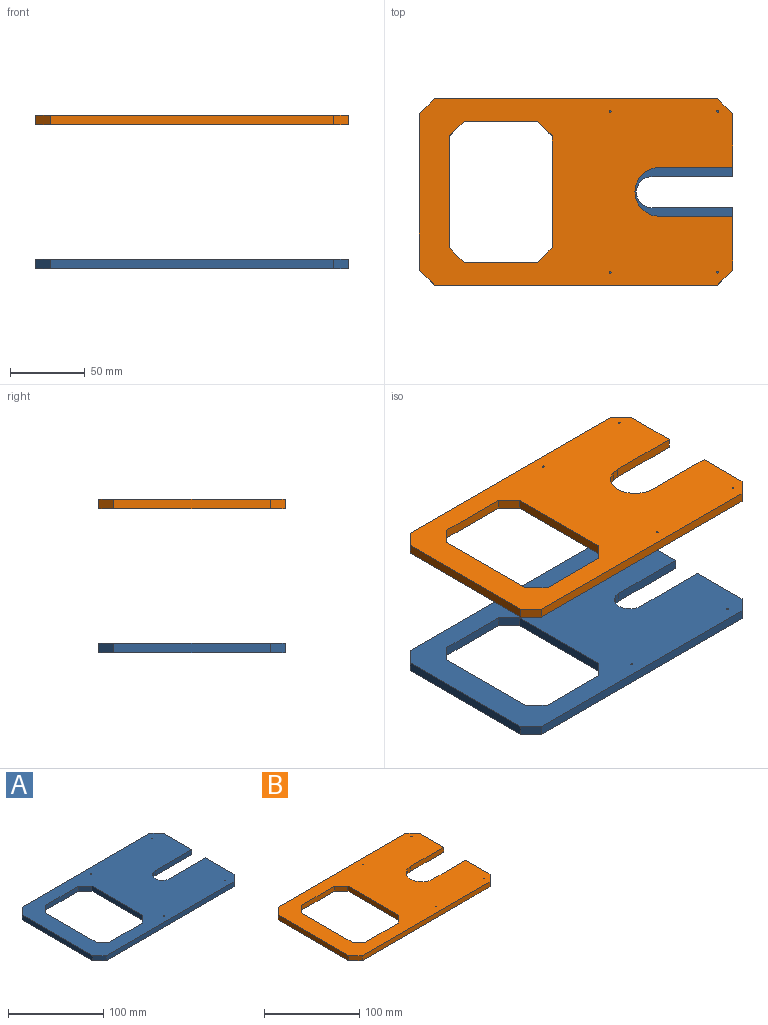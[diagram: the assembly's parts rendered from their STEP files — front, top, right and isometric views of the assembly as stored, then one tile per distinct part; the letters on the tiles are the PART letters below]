
ASSEMBLY  parts=2 mates=2
PART A: 73 faces, bbox 210x125x6.4 mm
  f0: plane 210x125mm, normal (0,0,1), area 18386mm2, adj f2,f3,f4,f5,f6,f7,f8,f9
  f1: plane 210x125mm, normal (0,0,-1), area 18386mm2, adj f2,f3,f4,f5,f6,f7,f8,f9
  f2: plane 42x6.4mm, normal (1,0,0), area 268.8mm2, adj f0,f1,f9,f63
  f3: plane 42x6.4mm, normal (1,0,0), area 268.8mm2, adj f0,f1,f8,f62
  f4: plane 190x6.4mm, normal (0,1,0), area 1216mm2, adj f0,f1,f63,f64
  f5: plane 105x6.4mm, normal (-1,0,0), area 672mm2, adj f0,f1,f61,f64
  f6: plane 190x6.4mm, normal (0,-1,0), area 1216mm2, adj f0,f1,f61,f62
  f7: plane 6.4x3.24mm, normal (0.16,0.99,0), area 21mm2, adj f0,f1,f8,f18
  f8: plane 54x6.4mm, normal (0,1,0), area 345.6mm2, adj f0,f1,f3,f7
  f9: plane 54x6.4mm, normal (0,-1,0), area 345.6mm2, adj f0,f1,f2,f10
  f10: plane 6.4x3.24mm, normal (0.16,-0.99,0), area 21mm2, adj f0,f1,f9,f11
  f11: plane 6.4x2.93mm, normal (0.45,-0.89,0), area 21mm2, adj f0,f1,f10,f12
  f12: plane 6.4x2.32mm, normal (0.71,-0.71,0), area 21mm2, adj f0,f1,f11,f13
  f13: plane 6.4x2.93mm, normal (0.89,-0.45,0), area 21mm2, adj f0,f1,f12,f14
  f14: plane 6.4x3.24mm, normal (0.99,-0.16,0), area 21mm2, adj f0,f1,f13,f15
  f15: plane 6.4x3.24mm, normal (0.99,0.16,0), area 21mm2, adj f0,f1,f14,f16
  f16: plane 6.4x2.93mm, normal (0.89,0.45,0), area 21mm2, adj f0,f1,f15,f17
  f17: plane 6.4x2.32mm, normal (0.71,0.71,0), area 21mm2, adj f0,f1,f16,f18
  f18: plane 6.4x2.93mm, normal (0.45,0.89,0), area 21mm2, adj f0,f1,f7,f17
  f19: plane 6.4x0.34mm, normal (-0.28,0.96,0), area 2.3mm2, adj f0,f1,f20,f29
  f20: plane 6.4x0.27mm, normal (-0.76,0.65,0), area 2.3mm2, adj f0,f1,f19,f21
  f21: plane 6.4x0.35mm, normal (-0.99,0.14,0), area 2.3mm2, adj f0,f1,f20,f22
  f22: plane 6.4x0.32mm, normal (-0.91,-0.42,0), area 2.3mm2, adj f0,f1,f21,f23
  f23: plane 6.4x0.3mm, normal (-0.54,-0.84,0), area 2.3mm2, adj f0,f1,f22,f24
  f24: plane 6.4x0.35mm, normal (0,-1,0), area 2.3mm2, adj f0,f1,f23,f25
  f25: plane 6.4x0.3mm, normal (0.54,-0.84,0), area 2.3mm2, adj f0,f1,f24,f26
  f26: plane 6.4x0.32mm, normal (0.91,-0.42,0), area 2.3mm2, adj f0,f1,f25,f27
  f27: plane 6.4x0.35mm, normal (0.99,0.14,0), area 2.3mm2, adj f0,f1,f26,f28
  f28: plane 6.4x0.27mm, normal (0.76,0.65,0), area 2.3mm2, adj f0,f1,f27,f29
  f29: plane 6.4x0.34mm, normal (0.28,0.96,0), area 2.3mm2, adj f0,f1,f19,f28
  f30: plane 6.4x0.37mm, normal (-0.31,0.95,0), area 2.5mm2, adj f0,f1,f31,f39
  f31: plane 6.4x0.32mm, normal (-0.81,0.59,0), area 2.5mm2, adj f0,f1,f30,f32
  f32: plane 6.4x0.39mm, normal (-1,0,0), area 2.5mm2, adj f0,f1,f31,f33
  f33: plane 6.4x0.32mm, normal (-0.81,-0.59,0), area 2.5mm2, adj f0,f1,f32,f34
  f34: plane 6.4x0.37mm, normal (-0.31,-0.95,0), area 2.5mm2, adj f0,f1,f33,f35
  f35: plane 6.4x0.37mm, normal (0.31,-0.95,0), area 2.5mm2, adj f0,f1,f34,f36
  f36: plane 6.4x0.32mm, normal (0.81,-0.59,0), area 2.5mm2, adj f0,f1,f35,f37
  f37: plane 6.4x0.39mm, normal (1,0,0), area 2.5mm2, adj f0,f1,f36,f38
  f38: plane 6.4x0.32mm, normal (0.81,0.59,0), area 2.5mm2, adj f0,f1,f37,f39
  f39: plane 6.4x0.37mm, normal (0.31,0.95,0), area 2.5mm2, adj f0,f1,f30,f38
  f40: plane 6.4x0.39mm, normal (-1,0,0), area 2.5mm2, adj f0,f1,f41,f49
  f41: plane 6.4x0.32mm, normal (-0.81,-0.59,0), area 2.5mm2, adj f0,f1,f40,f42
  f42: plane 6.4x0.37mm, normal (-0.31,-0.95,0), area 2.5mm2, adj f0,f1,f41,f43
  f43: plane 6.4x0.37mm, normal (0.31,-0.95,0), area 2.5mm2, adj f0,f1,f42,f44
  f44: plane 6.4x0.32mm, normal (0.81,-0.59,0), area 2.5mm2, adj f0,f1,f43,f45
  f45: plane 6.4x0.39mm, normal (1,0,0), area 2.5mm2, adj f0,f1,f44,f46
  f46: plane 6.4x0.32mm, normal (0.81,0.59,0), area 2.5mm2, adj f0,f1,f45,f47
  f47: plane 6.4x0.37mm, normal (0.31,0.95,0), area 2.5mm2, adj f0,f1,f46,f48
  f48: plane 6.4x0.37mm, normal (-0.31,0.95,0), area 2.5mm2, adj f0,f1,f47,f49
  f49: plane 6.4x0.32mm, normal (-0.81,0.59,0), area 2.5mm2, adj f0,f1,f40,f48
  f50: plane 6.4x0.27mm, normal (-0.76,-0.65,0), area 2.3mm2, adj f0,f1,f51,f60
  f51: plane 6.4x0.34mm, normal (-0.28,-0.96,0), area 2.3mm2, adj f0,f1,f50,f52
  f52: plane 6.4x0.34mm, normal (0.28,-0.96,0), area 2.3mm2, adj f0,f1,f51,f53
  f53: plane 6.4x0.27mm, normal (0.76,-0.65,0), area 2.3mm2, adj f0,f1,f52,f54
  f54: plane 6.4x0.35mm, normal (0.99,-0.14,0), area 2.3mm2, adj f0,f1,f53,f55
  f55: plane 6.4x0.32mm, normal (0.91,0.42,0), area 2.3mm2, adj f0,f1,f54,f56
  f56: plane 6.4x0.3mm, normal (0.54,0.84,0), area 2.3mm2, adj f0,f1,f55,f57
  f57: plane 6.4x0.35mm, normal (0,1,0), area 2.3mm2, adj f0,f1,f56,f58
  f58: plane 6.4x0.3mm, normal (-0.54,0.84,0), area 2.3mm2, adj f0,f1,f57,f59
  f59: plane 6.4x0.32mm, normal (-0.91,0.42,0), area 2.3mm2, adj f0,f1,f58,f60
  f60: plane 6.4x0.35mm, normal (-0.99,-0.14,0), area 2.3mm2, adj f0,f1,f50,f59
  f61: plane 10x10mm, normal (-0.71,-0.71,0), area 90.5mm2, adj f0,f1,f5,f6
  f62: plane 10x10mm, normal (0.71,-0.71,0), area 90.5mm2, adj f0,f1,f3,f6
  f63: plane 10x10mm, normal (0.71,0.71,0), area 90.5mm2, adj f0,f1,f2,f4
  f64: plane 10x10mm, normal (-0.71,0.71,0), area 90.5mm2, adj f0,f1,f4,f5
  f65: plane 75x6.4mm, normal (-1,0,0), area 480mm2, adj f0,f1,f70,f71
  f66: plane 49x6.4mm, normal (0,1,0), area 313.6mm2, adj f0,f1,f69,f70
  f67: plane 75x6.4mm, normal (1,0,0), area 480mm2, adj f0,f1,f69,f72
  f68: plane 49x6.4mm, normal (0,-1,0), area 313.6mm2, adj f0,f1,f71,f72
  f69: plane 10x10mm, normal (0.71,0.71,0), area 90.5mm2, adj f0,f1,f66,f67
  f70: plane 10x10mm, normal (-0.71,0.71,0), area 90.5mm2, adj f0,f1,f65,f66
  f71: plane 10x10mm, normal (-0.71,-0.71,0), area 90.5mm2, adj f0,f1,f65,f68
  f72: plane 10x10mm, normal (0.71,-0.71,0), area 90.5mm2, adj f0,f1,f67,f68
PART B: 73 faces, bbox 210x125x6.4 mm
  f0: plane 210x125mm, normal (0,0,1), area 17652.7mm2, adj f2,f3,f4,f5,f6,f7,f8,f9
  f1: plane 210x125mm, normal (0,0,-1), area 17652.7mm2, adj f2,f3,f4,f5,f6,f7,f8,f9
  f2: plane 36x6.4mm, normal (1,0,0), area 230.4mm2, adj f0,f1,f9,f63
  f3: plane 36x6.4mm, normal (1,0,0), area 230.4mm2, adj f0,f1,f8,f62
  f4: plane 190x6.4mm, normal (0,1,0), area 1216mm2, adj f0,f1,f63,f64
  f5: plane 105x6.4mm, normal (-1,0,0), area 672mm2, adj f0,f1,f61,f64
  f6: plane 190x6.4mm, normal (0,-1,0), area 1216mm2, adj f0,f1,f61,f62
  f7: plane 6.4x5.1mm, normal (0.16,0.99,0), area 33mm2, adj f0,f1,f8,f18
  f8: plane 49x6.4mm, normal (0,1,0), area 313.6mm2, adj f0,f1,f3,f7
  f9: plane 49x6.4mm, normal (0,-1,0), area 313.6mm2, adj f0,f1,f2,f10
  f10: plane 6.4x5.1mm, normal (0.16,-0.99,0), area 33mm2, adj f0,f1,f9,f11
  f11: plane 6.4x4.6mm, normal (0.45,-0.89,0), area 33mm2, adj f0,f1,f10,f12
  f12: plane 6.4x3.65mm, normal (0.71,-0.71,0), area 33mm2, adj f0,f1,f11,f13
  f13: plane 6.4x4.6mm, normal (0.89,-0.45,0), area 33mm2, adj f0,f1,f12,f14
  f14: plane 6.4x5.1mm, normal (0.99,-0.16,0), area 33mm2, adj f0,f1,f13,f15
  f15: plane 6.4x5.1mm, normal (0.99,0.16,0), area 33mm2, adj f0,f1,f14,f16
  f16: plane 6.4x4.6mm, normal (0.89,0.45,0), area 33mm2, adj f0,f1,f15,f17
  f17: plane 6.4x3.65mm, normal (0.71,0.71,0), area 33mm2, adj f0,f1,f16,f18
  f18: plane 6.4x4.6mm, normal (0.45,0.89,0), area 33mm2, adj f0,f1,f7,f17
  f19: plane 6.4x0.27mm, normal (-0.76,0.65,0), area 2.3mm2, adj f0,f1,f20,f28
  f20: plane 6.4x0.35mm, normal (-0.99,0.14,0), area 2.3mm2, adj f0,f1,f19,f21
  f21: plane 6.4x0.32mm, normal (-0.91,-0.42,0), area 2.3mm2, adj f0,f1,f20,f22
  f22: plane 6.4x0.3mm, normal (-0.54,-0.84,0), area 2.3mm2, adj f0,f1,f21,f23
  f23: plane 6.4x0.35mm, normal (0,-1,0), area 2.3mm2, adj f0,f1,f22,f24
  f24: plane 6.4x0.3mm, normal (0.54,-0.84,0), area 2.3mm2, adj f0,f1,f23,f25
  f25: plane 6.4x0.32mm, normal (0.91,-0.42,0), area 2.3mm2, adj f0,f1,f24,f26
  f26: plane 6.4x0.35mm, normal (0.99,0.14,0), area 2.3mm2, adj f0,f1,f25,f27
  f27: plane 6.4x0.27mm, normal (0.76,0.65,0), area 2.3mm2, adj f0,f1,f26,f29
  f28: plane 6.4x0.34mm, normal (-0.28,0.96,0), area 2.3mm2, adj f0,f1,f19,f29
  f29: plane 6.4x0.34mm, normal (0.28,0.96,0), area 2.3mm2, adj f0,f1,f27,f28
  f30: plane 6.4x0.37mm, normal (-0.31,0.95,0), area 2.5mm2, adj f0,f1,f31,f39
  f31: plane 6.4x0.32mm, normal (-0.81,0.59,0), area 2.5mm2, adj f0,f1,f30,f32
  f32: plane 6.4x0.39mm, normal (-1,0,0), area 2.5mm2, adj f0,f1,f31,f33
  f33: plane 6.4x0.32mm, normal (-0.81,-0.59,0), area 2.5mm2, adj f0,f1,f32,f34
  f34: plane 6.4x0.37mm, normal (-0.31,-0.95,0), area 2.5mm2, adj f0,f1,f33,f35
  f35: plane 6.4x0.37mm, normal (0.31,-0.95,0), area 2.5mm2, adj f0,f1,f34,f36
  f36: plane 6.4x0.32mm, normal (0.81,-0.59,0), area 2.5mm2, adj f0,f1,f35,f37
  f37: plane 6.4x0.39mm, normal (1,0,0), area 2.5mm2, adj f0,f1,f36,f38
  f38: plane 6.4x0.32mm, normal (0.81,0.59,0), area 2.5mm2, adj f0,f1,f37,f39
  f39: plane 6.4x0.37mm, normal (0.31,0.95,0), area 2.5mm2, adj f0,f1,f30,f38
  f40: plane 6.4x0.32mm, normal (-0.81,-0.59,0), area 2.5mm2, adj f0,f1,f41,f48
  f41: plane 6.4x0.37mm, normal (-0.31,-0.95,0), area 2.5mm2, adj f0,f1,f40,f42
  f42: plane 6.4x0.37mm, normal (0.31,-0.95,0), area 2.5mm2, adj f0,f1,f41,f43
  f43: plane 6.4x0.32mm, normal (0.81,-0.59,0), area 2.5mm2, adj f0,f1,f42,f44
  f44: plane 6.4x0.39mm, normal (1,0,0), area 2.5mm2, adj f0,f1,f43,f45
  f45: plane 6.4x0.32mm, normal (0.81,0.59,0), area 2.5mm2, adj f0,f1,f44,f46
  f46: plane 6.4x0.37mm, normal (0.31,0.95,0), area 2.5mm2, adj f0,f1,f45,f47
  f47: plane 6.4x0.37mm, normal (-0.31,0.95,0), area 2.5mm2, adj f0,f1,f46,f49
  f48: plane 6.4x0.39mm, normal (-1,0,0), area 2.5mm2, adj f0,f1,f40,f49
  f49: plane 6.4x0.32mm, normal (-0.81,0.59,0), area 2.5mm2, adj f0,f1,f47,f48
  f50: plane 6.4x0.27mm, normal (-0.76,-0.65,0), area 2.3mm2, adj f0,f1,f51,f60
  f51: plane 6.4x0.34mm, normal (-0.28,-0.96,0), area 2.3mm2, adj f0,f1,f50,f52
  f52: plane 6.4x0.34mm, normal (0.28,-0.96,0), area 2.3mm2, adj f0,f1,f51,f53
  f53: plane 6.4x0.27mm, normal (0.76,-0.65,0), area 2.3mm2, adj f0,f1,f52,f54
  f54: plane 6.4x0.35mm, normal (0.99,-0.14,0), area 2.3mm2, adj f0,f1,f53,f55
  f55: plane 6.4x0.32mm, normal (0.91,0.42,0), area 2.3mm2, adj f0,f1,f54,f56
  f56: plane 6.4x0.3mm, normal (0.54,0.84,0), area 2.3mm2, adj f0,f1,f55,f57
  f57: plane 6.4x0.35mm, normal (0,1,0), area 2.3mm2, adj f0,f1,f56,f58
  f58: plane 6.4x0.3mm, normal (-0.54,0.84,0), area 2.3mm2, adj f0,f1,f57,f59
  f59: plane 6.4x0.32mm, normal (-0.91,0.42,0), area 2.3mm2, adj f0,f1,f58,f60
  f60: plane 6.4x0.35mm, normal (-0.99,-0.14,0), area 2.3mm2, adj f0,f1,f50,f59
  f61: plane 10x10mm, normal (-0.71,-0.71,0), area 90.5mm2, adj f0,f1,f5,f6
  f62: plane 10x10mm, normal (0.71,-0.71,0), area 90.5mm2, adj f0,f1,f3,f6
  f63: plane 10x10mm, normal (0.71,0.71,0), area 90.5mm2, adj f0,f1,f2,f4
  f64: plane 10x10mm, normal (-0.71,0.71,0), area 90.5mm2, adj f0,f1,f4,f5
  f65: plane 75x6.4mm, normal (-1,0,0), area 480mm2, adj f0,f1,f70,f71
  f66: plane 49x6.4mm, normal (0,1,0), area 313.6mm2, adj f0,f1,f69,f70
  f67: plane 75x6.4mm, normal (1,0,0), area 480mm2, adj f0,f1,f69,f72
  f68: plane 49x6.4mm, normal (0,-1,0), area 313.6mm2, adj f0,f1,f71,f72
  f69: plane 10x10mm, normal (0.71,0.71,0), area 90.5mm2, adj f0,f1,f66,f67
  f70: plane 10x10mm, normal (-0.71,0.71,0), area 90.5mm2, adj f0,f1,f65,f66
  f71: plane 10x10mm, normal (-0.71,-0.71,0), area 90.5mm2, adj f0,f1,f65,f68
  f72: plane 10x10mm, normal (0.71,-0.71,0), area 90.5mm2, adj f0,f1,f67,f68
PLACE A t=(-62.96,-79.59,-124.31)mm
PLACE B t=(-62.96,-79.59,-27.81)mm
MATE planar A.f3 <-> B.f3  axis (1,0,0) through (42.04,-111.09,-121.11)mm
MATE planar A.f6 <-> B.f6  axis (0,-1,0) through (-62.96,-142.09,-121.11)mm
